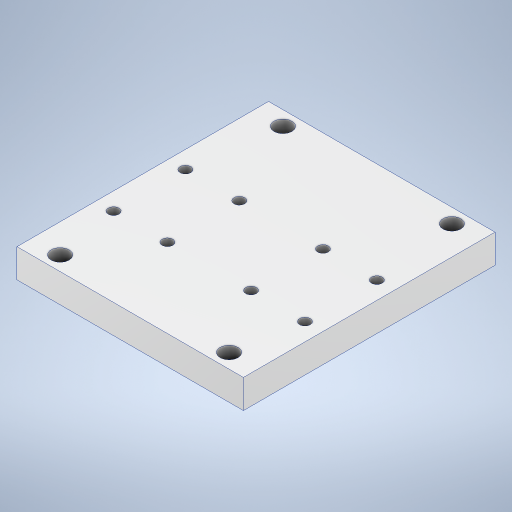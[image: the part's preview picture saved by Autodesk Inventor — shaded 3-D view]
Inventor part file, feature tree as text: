
AUTODESK INVENTOR PART (.ipt)
format: ipt  version: 2023 (Build 270158000, 158)  size: 264,192 bytes
history: native  units: mm
features: sketch x3, hole x2, extrude x1
ambient origin geometry x8: Origin, YZ Plane, XZ Plane, XY Plane, X Axis, Y Axis, Z Axis, Center Point
bodies: Solid1 (feature_tree)
feature tree (6):
  extrude  "Extrusion1"  Depth=63.0mm
  hole  "Hole1"  [1 undecoded]
  hole  "Hole2"  [1 undecoded]
  sketch  "Sketch1"  dims[d0=70.0mm d1=63.0mm]
  sketch  "Sketch2"  dims[d2=8.0mm d3=0.0mm d4=70.0mm]
  sketch  "Sketch3"  dims[d5=63.0mm d6=20.0mm d8=15.0mm d9=20.0mm d11=20.0mm d16=20.0mm d18=20.0mm d19=20.0mm d21=15.0mm d24=23.25mm d25=0.0mm d26=28.0mm d27=53.25mm d28=-4.875mm d29=3.0mm d30=6.0mm d31=4.0mm d32=2.0mm d33=90.0deg d34=0.5mm d35=20.594885mm d36=20.0mm d38=47.0mm d39=20.0mm d41=62.0mm d44=63.0mm d45=70.0mm d46=4.0mm d47=8.0mm d48=5.0mm d49=10.0mm d50=3.023mm d51=2.0mm d52=14.3117mm d53=0.5mm d54=20.594885mm]
note: 2 required parameter values undecoded (feature->parameter linkage not recoverable at this tier; creation-order binding heuristic only, values carry confidence <= 0.55)
